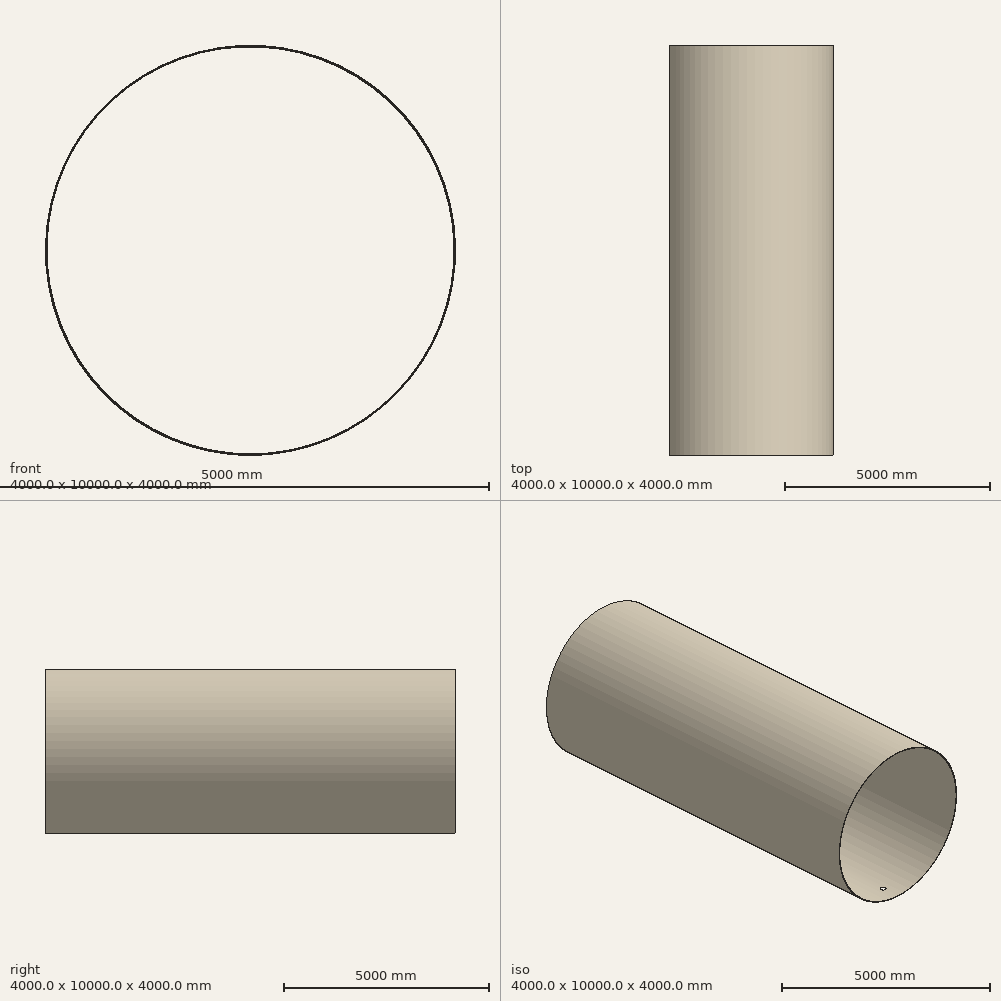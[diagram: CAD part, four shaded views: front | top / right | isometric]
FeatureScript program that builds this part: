
annotation { "Feature Type Name" : "Feature", "Feature Type Description" : "" }
export const myFeature = defineFeature(function(context is Context, id is Id, definition is map)
    precondition{}
    {
        {
            var Q0;
            Q0=qCreatedBy(makeId("Front.planeOp"),FACE);
            var sketch = newSketch(context, id + "F0", { "sketchPlane" : qUnion([Q0])});
            skCircle(sketch, "E0", {"center": v(0, 0) * mm, "radius": 2000 * mm});
            skCircle(sketch, "E1", {"center": v(0, 0) * mm, "radius": 1985 * mm});
            skSolve(sketch);
        }
        {
            var Q0;
            Q0=makeQuery(id+"F0.imprint","IMPRINT",FACE,{"disambiguationData":[TD([[makeQuery(id+"F0.imprint","IMPRINT",EDGE,{"derivedFrom":sQuery(id+"F0.wireOp",EDGE,"E0")}),1.0]])]});
            extrude(context, id + "F1", {"entities" : qUnion([Q0]), "endBound" : BoundingType.SYMMETRIC, "depth" : 10000 * mm});
        }
        {
            var Q0;
            Q0=qCreatedBy(makeId("Top.planeOp"),FACE);
            cPlane(context, id + "F2", {"entities" : qUnion([Q0]), "cplaneType" : CPlaneType.OFFSET, "offset" : 1000 * mm, "width" : 150 * mm, "height" : 150 * mm});
        }
        {
            var Q0;
            Q0=qCreatedBy(id+"F2.planeOp",FACE);
            var sketch = newSketch(context, id + "F3", { "sketchPlane" : qUnion([Q0])});
            skPoint(sketch, "E2", {"position": v(0, -4500) * mm});
            skSolve(sketch);
        }
        {
            var Q0;
            Q0=sQuery(id+"F3.wireOp",VERTEX,"E2");
            var Q1;
            Q1=makeQuery(id+"F1.opExtrude","SWEPT_BODY",BODY,{"disambiguationData":[OSD([sQuery(id+"F0.wireOp",EDGE,"E0"),sQuery(id+"F0.wireOp",EDGE,"E1")])]});
            hole(context, id + "F4", {"style" : HoleStyle.SIMPLE, "holeDiameter" : 140 * mm, "endStyle" : HoleEndStyle.BLIND, "holeDepth" : 140 * mm, "locations" : qUnion([Q0]), "scope" : qUnion([Q1])});
        }
        {
            var Q0;
            Q0=makeQuery(id+"F1.opExtrude","CAP_FACE",FACE,{"disambiguationData":[OSD([sQuery(id+"F0.wireOp",EDGE,"E0"),sQuery(id+"F0.wireOp",EDGE,"E1")])],"isStart":false});
            chamfer(context, id + "F5", {"entities" : qUnion([Q0]), "width" : 5 * mm, "tangentPropagation" : true});
        }
        {
            var Q0;
            Q0=makeQuery(id+"F1.opExtrude","CAP_EDGE",EDGE,{"disambiguationData":[OSD([sQuery(id+"F0.wireOp",EDGE,"E0")])],"isStart":true});
            chamfer(context, id + "F6", {"entities" : qUnion([Q0]), "width" : 5 * mm, "tangentPropagation" : true});
        }
        {
            var Q0;
            Q0=makeQuery(id+"F1.opExtrude","CAP_EDGE",EDGE,{"disambiguationData":[OSD([sQuery(id+"F0.wireOp",EDGE,"E1")])],"isStart":true});
            chamfer(context, id + "F7", {"entities" : qUnion([Q0]), "width" : 5 * mm, "tangentPropagation" : true});
        }
    });
